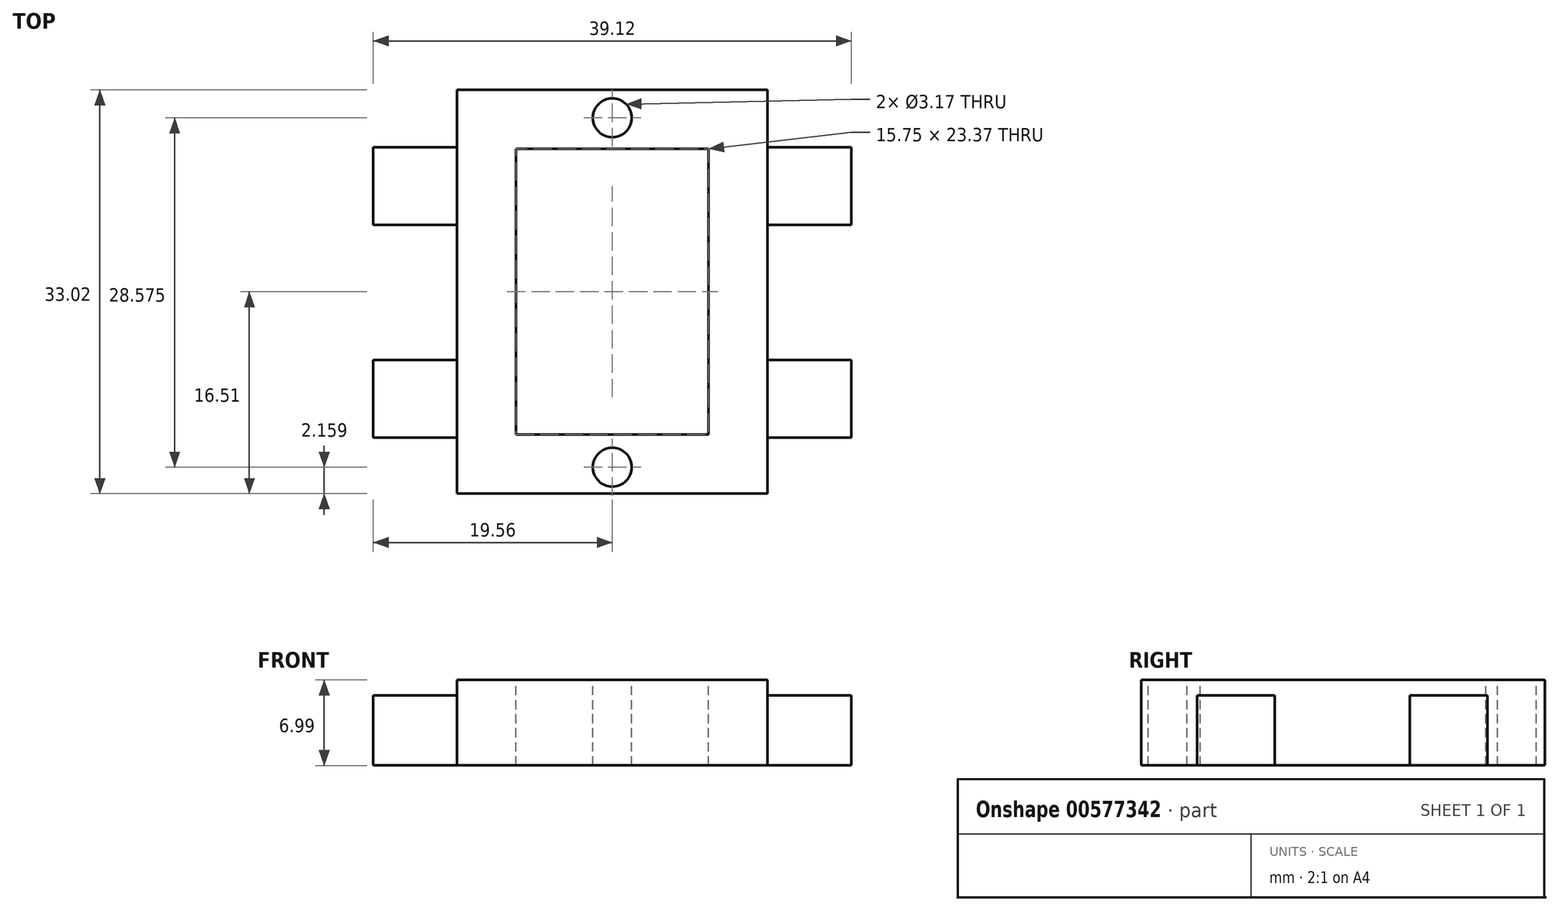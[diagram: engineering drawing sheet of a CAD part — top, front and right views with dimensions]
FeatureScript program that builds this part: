
annotation { "Feature Type Name" : "Feature", "Feature Type Description" : "" }
export const myFeature = defineFeature(function(context is Context, id is Id, definition is map)
    precondition{}
    {
        {
            var Q0;
            Q0=qCreatedBy(makeId("Top.planeOp"),FACE);
            var sketch = newSketch(context, id + "F0", { "sketchPlane" : qUnion([Q0])});
            skLineSegment(sketch, "E0.bottom", {"start": v(-12.7, 16.51) * mm, "end": v(12.7, 16.51) * mm});
            skLineSegment(sketch, "E0.top", {"start": v(-12.7, -16.51) * mm, "end": v(12.7, -16.51) * mm});
            skLineSegment(sketch, "E0.left", {"start": v(-12.7, 16.51) * mm, "end": v(-12.7, -16.51) * mm});
            skLineSegment(sketch, "E0.right", {"start": v(12.7, 16.51) * mm, "end": v(12.7, -16.51) * mm});
            skLineSegment(sketch, "E1.0", {"start": v(-7.87, 11.68) * mm, "end": v(7.87, 11.68) * mm});
            skLineSegment(sketch, "E1.1", {"start": v(-7.87, 11.68) * mm, "end": v(-7.87, -11.68) * mm});
            skLineSegment(sketch, "E1.2", {"start": v(-7.87, -11.68) * mm, "end": v(7.87, -11.68) * mm});
            skLineSegment(sketch, "E1.3", {"start": v(7.87, 11.68) * mm, "end": v(7.87, -11.68) * mm});
            skCircle(sketch, "E2", {"center": v(0, 14.22) * mm, "radius": 1.59 * mm});
            skCircle(sketch, "E3", {"center": v(0, -14.35) * mm, "radius": 1.59 * mm});
            skLineSegment(sketch, "E4.bottom", {"start": v(-19.56, 11.81) * mm, "end": v(-12.7, 11.81) * mm});
            skLineSegment(sketch, "E4.top", {"start": v(-19.56, 5.46) * mm, "end": v(-12.7, 5.46) * mm});
            skLineSegment(sketch, "E4.left", {"start": v(-19.56, 11.81) * mm, "end": v(-19.56, 5.46) * mm});
            skLineSegment(sketch, "E4.right", {"start": v(-12.7, 11.81) * mm, "end": v(-12.7, 5.46) * mm});
            skPoint(sketch, "E5.oppositeSnap0", {"position": v(-16.13, 5.46) * mm});
            skLineSegment(sketch, "E5.bottom", {"start": v(12.7, 11.81) * mm, "end": v(19.56, 11.81) * mm});
            skLineSegment(sketch, "E5.top", {"start": v(12.7, 5.46) * mm, "end": v(19.56, 5.46) * mm});
            skLineSegment(sketch, "E5.left", {"start": v(12.7, 11.81) * mm, "end": v(12.7, 5.46) * mm});
            skLineSegment(sketch, "E5.right", {"start": v(19.56, 11.81) * mm, "end": v(19.56, 5.46) * mm});
            skLineSegment(sketch, "E6.bottom", {"start": v(-12.7, -5.59) * mm, "end": v(-19.56, -5.59) * mm});
            skLineSegment(sketch, "E6.top", {"start": v(-12.7, -11.94) * mm, "end": v(-19.56, -11.94) * mm});
            skLineSegment(sketch, "E6.left", {"start": v(-12.7, -5.59) * mm, "end": v(-12.7, -11.94) * mm});
            skLineSegment(sketch, "E6.right", {"start": v(-19.56, -5.59) * mm, "end": v(-19.56, -11.94) * mm});
            skLineSegment(sketch, "E7.bottom", {"start": v(12.7, -5.59) * mm, "end": v(19.56, -5.59) * mm});
            skLineSegment(sketch, "E7.top", {"start": v(12.7, -11.94) * mm, "end": v(19.56, -11.94) * mm});
            skLineSegment(sketch, "E7.left", {"start": v(12.7, -5.59) * mm, "end": v(12.7, -11.94) * mm});
            skLineSegment(sketch, "E7.right", {"start": v(19.56, -5.59) * mm, "end": v(19.56, -11.94) * mm});
            skSolve(sketch);
        }
        {
            var Q0;
            Q0 = qSketchRegion(id + "F0", true);
            extrude(context, id + "F1", {"entities" : qUnion([Q0]), "oppositeDirection" : true, "depth" : 5.7 * mm, "offsetDistance" : 25.4 * mm});
        }
        {
            var Q0;
            Q0=makeQuery(id+"F1.opExtrude","CAP_FACE",FACE,{"disambiguationData":[OSD([sQuery(id+"F0.wireOp",EDGE,"E0.bottom"),sQuery(id+"F0.wireOp",EDGE,"E0.top"),sQuery(id+"F0.wireOp",EDGE,"E0.left"),sQuery(id+"F0.wireOp",EDGE,"E0.right"),sQuery(id+"F0.wireOp",EDGE,"E1.0"),sQuery(id+"F0.wireOp",EDGE,"E1.1"),sQuery(id+"F0.wireOp",EDGE,"E1.2"),sQuery(id+"F0.wireOp",EDGE,"E1.3"),sQuery(id+"F0.wireOp",EDGE,"E2"),sQuery(id+"F0.wireOp",EDGE,"E3"),sQuery(id+"F0.wireOp",EDGE,"E4.bottom"),sQuery(id+"F0.wireOp",EDGE,"E4.top"),sQuery(id+"F0.wireOp",EDGE,"E4.left"),sQuery(id+"F0.wireOp",EDGE,"E5.bottom"),sQuery(id+"F0.wireOp",EDGE,"E5.top"),sQuery(id+"F0.wireOp",EDGE,"E5.right"),sQuery(id+"F0.wireOp",EDGE,"E6.bottom"),sQuery(id+"F0.wireOp",EDGE,"E6.top"),sQuery(id+"F0.wireOp",EDGE,"E6.right"),sQuery(id+"F0.wireOp",EDGE,"E7.bottom"),sQuery(id+"F0.wireOp",EDGE,"E7.top"),sQuery(id+"F0.wireOp",EDGE,"E7.right")])],"isStart":true});
            var sketch = newSketch(context, id + "F2", { "sketchPlane" : qUnion([Q0])});
            skLineSegment(sketch, "E8.bottom", {"start": v(-12.7, 16.51) * mm, "end": v(12.7, 16.51) * mm});
            skLineSegment(sketch, "E8.top", {"start": v(-12.7, -16.51) * mm, "end": v(12.7, -16.51) * mm});
            skLineSegment(sketch, "E8.left", {"start": v(-12.7, 16.51) * mm, "end": v(-12.7, -16.51) * mm});
            skLineSegment(sketch, "E8.right", {"start": v(12.7, 16.51) * mm, "end": v(12.7, -16.51) * mm});
            skLineSegment(sketch, "E9.0", {"start": v(-7.87, 11.68) * mm, "end": v(7.87, 11.68) * mm});
            skLineSegment(sketch, "E10.0", {"start": v(-7.87, 11.68) * mm, "end": v(-7.87, -11.68) * mm});
            skLineSegment(sketch, "E11.0", {"start": v(-7.87, -11.68) * mm, "end": v(7.87, -11.68) * mm});
            skLineSegment(sketch, "E12.0", {"start": v(7.87, 11.68) * mm, "end": v(7.87, -11.68) * mm});
            skCircle(sketch, "E13.0", {"center": v(0, 14.22) * mm, "radius": 1.59 * mm});
            skCircle(sketch, "E14.0", {"center": v(0, -14.35) * mm, "radius": 1.59 * mm});
            skSolve(sketch);
        }
        {
            var Q0;
            Q0 = qSketchRegion(id + "F2", true);
            extrude(context, id + "F3", {"entities" : qUnion([Q0]), "operationType" : NewBodyOperationType.ADD, "depth" : 1.27 * mm, "offsetDistance" : 25.4 * mm});
        }
    });
